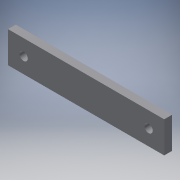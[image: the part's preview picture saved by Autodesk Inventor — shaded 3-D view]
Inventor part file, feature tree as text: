
AUTODESK INVENTOR PART (.ipt)
format: ipt  version: 2016 (Build 200138000, 138)  size: 95,744 bytes
history: native  units: in
note: dims shown in document units (in); Inventor stores cm internally (conversion verified against a paired STEP export)
features: extrude x1, sketch x1
ambient origin geometry x8: Origin, YZ Plane, XZ Plane, XY Plane, X Axis, Y Axis, Z Axis, Center Point
bodies: Solid1 (feature_tree)
feature tree (2):
  extrude  "Extrusion1"  Depth=1.0in
  sketch  "Sketch1"  dims[d0=6.0in d1=1.0in d2=0.2656in d3=0.2656in d4=0.5in d5=0.5in d6=0.5in d7=0.5in d8=0.25in d9=0.0in]
